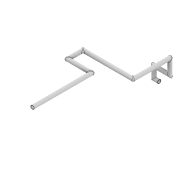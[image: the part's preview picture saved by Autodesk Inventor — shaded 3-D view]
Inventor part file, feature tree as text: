
AUTODESK INVENTOR PART (.ipt)
format: ipt  version: 2021 (Build 250183000, 183)  size: 184,320 bytes
history: native  units: mm
features: sketch x2, other x1, sweep x1, fillet x1
ambient origin geometry x8: Origin, YZ Plane, XZ Plane, XY Plane, X Axis, Y Axis, Z Axis, Center Point
bodies: Body1 (feature_tree)
feature tree (5):
  sketch  "Эскиз1"
  other  "РабПлоскость1"
  sweep  "Сдвиг2"
  fillet  "Сопряжение1"  Radius=53.0mm
  sketch  "3D эскиз2"
